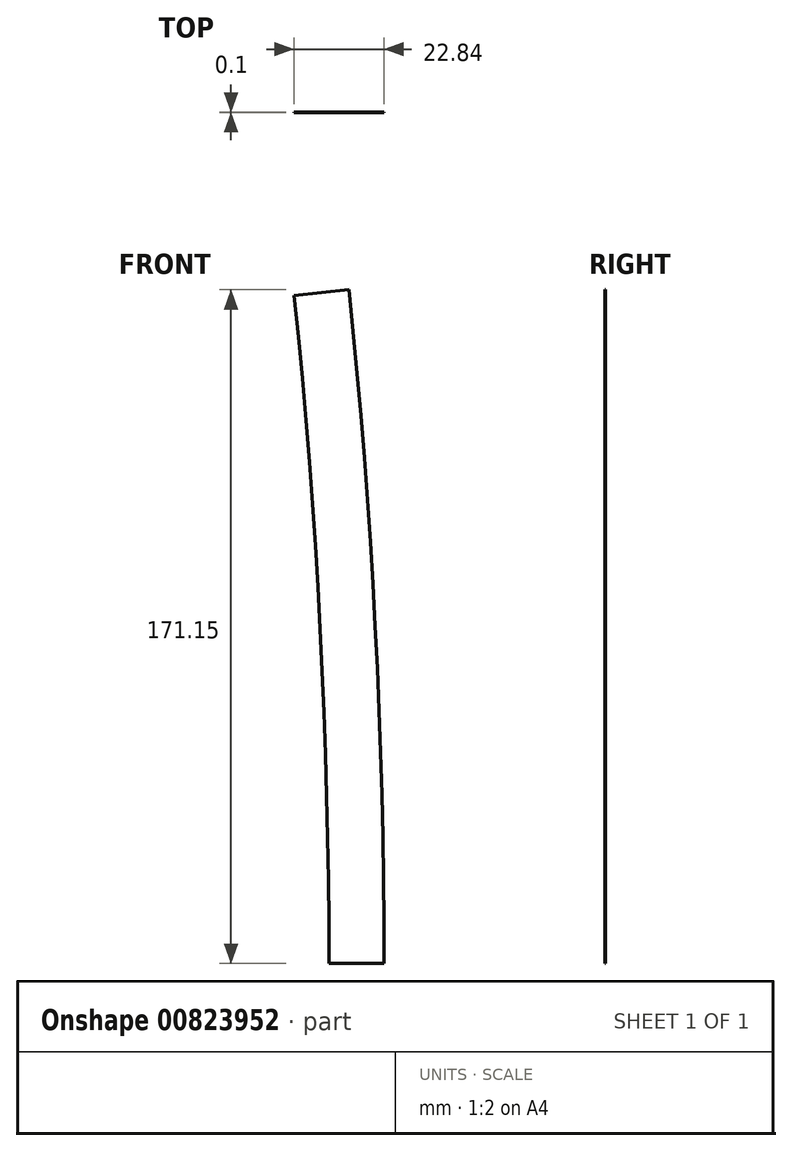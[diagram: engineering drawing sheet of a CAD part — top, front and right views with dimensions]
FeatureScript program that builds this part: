
annotation { "Feature Type Name" : "Feature", "Feature Type Description" : "" }
export const myFeature = defineFeature(function(context is Context, id is Id, definition is map)
    precondition{}
    {
        {
            var Q0;
            Q0=qCreatedBy(makeId("Front.planeOp"),FACE);
            var sketch = newSketch(context, id + "F0", { "sketchPlane" : qUnion([Q0])});
            skLineSegment(sketch, "E0", {"start": v(-14, 0) * mm, "end": v(0, 0) * mm});
            skLineSegment(sketch, "E1", {"start": v(-22.84, 169.7) * mm, "end": v(-8.91, 171.15) * mm});
            skArc(sketch, "E2", {"start": v(0, 0) * mm, "mid": v(-2.23, 85.69) * mm, "end": v(-8.91, 171.15) * mm});
            skArc(sketch, "E3", {"start": v(-14, 0) * mm, "mid": v(-16.21, 84.96) * mm, "end": v(-22.84, 169.7) * mm});
            skLineSegment(sketch, "E4", {"start": v(-1647.34, 0) * mm, "end": v(-8.91, 171.15) * mm, "construction": true});
            skSolve(sketch);
        }
        {
            var Q0;
            Q0=makeQuery(id+"F0.imprint","IMPRINT",FACE,{"disambiguationData":[TD([[makeQuery(id+"F0.imprint","IMPRINT",EDGE,{"derivedFrom":sQuery(id+"F0.wireOp",EDGE,"E0")}),1.0]])]});
            extrude(context, id + "F1", {"entities" : qUnion([Q0]), "depth" : 0.1 * mm, "offsetDistance" : 25 * mm});
        }
    });
